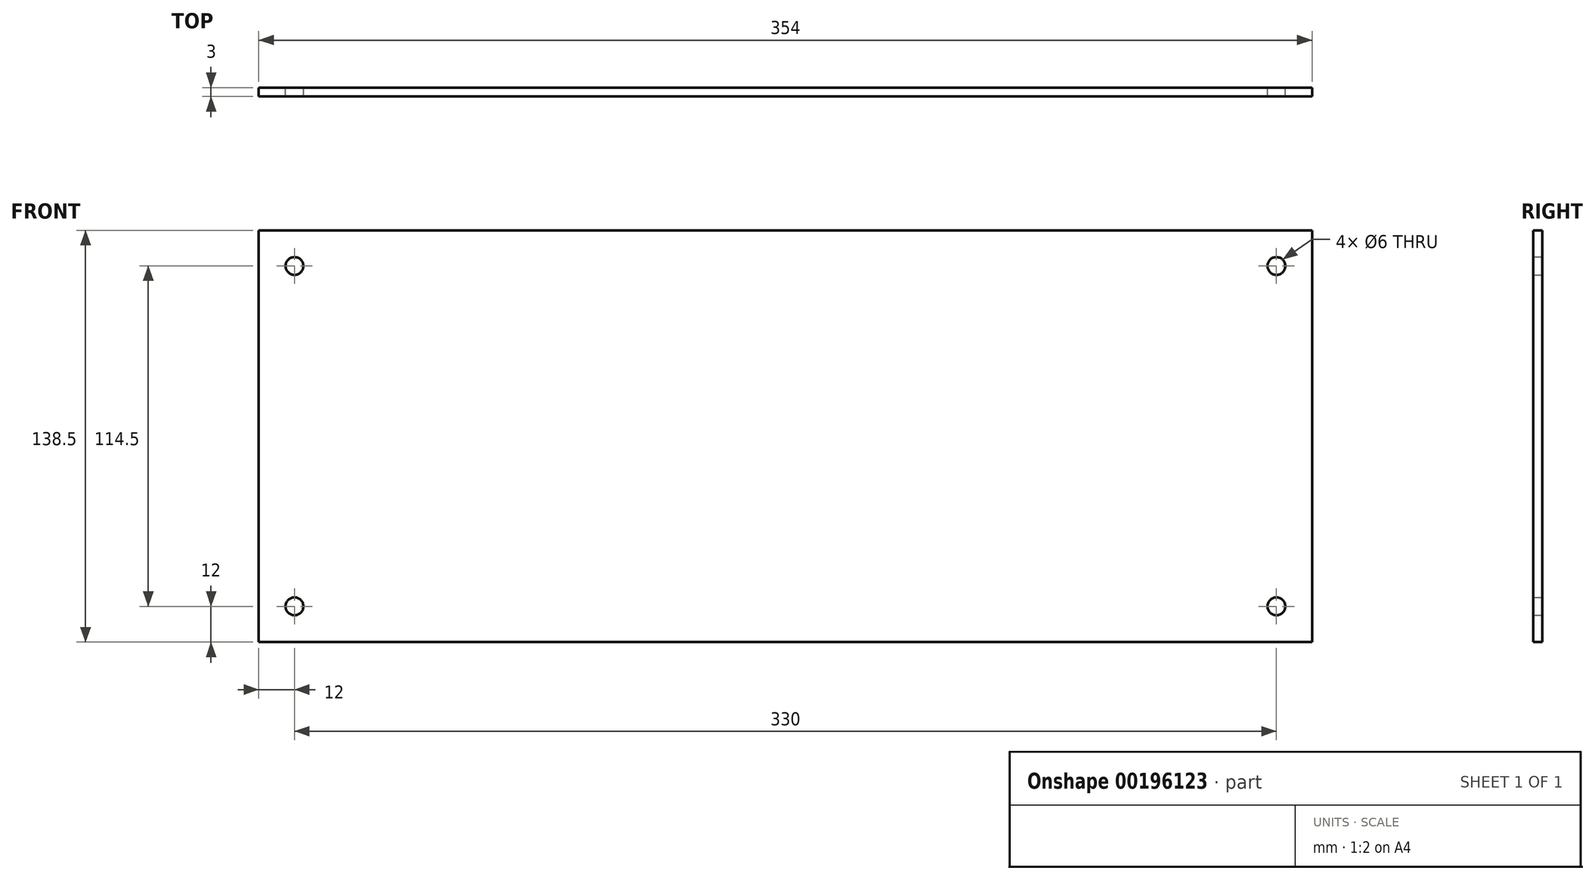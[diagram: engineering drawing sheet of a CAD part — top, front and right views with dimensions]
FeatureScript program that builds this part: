
annotation { "Feature Type Name" : "Feature", "Feature Type Description" : "" }
export const myFeature = defineFeature(function(context is Context, id is Id, definition is map)
    precondition{}
    {
        {
            var Q0;
            Q0=qCreatedBy(makeId("Front.planeOp"),FACE);
            var sketch = newSketch(context, id + "F0", { "sketchPlane" : qUnion([Q0])});
            skLineSegment(sketch, "E0.bottom", {"start": v(177, -69.25) * mm, "end": v(-177, -69.25) * mm});
            skLineSegment(sketch, "E0.top", {"start": v(177, 69.25) * mm, "end": v(-177, 69.25) * mm});
            skLineSegment(sketch, "E0.left", {"start": v(177, -69.25) * mm, "end": v(177, 69.25) * mm});
            skLineSegment(sketch, "E0.right", {"start": v(-177, -69.25) * mm, "end": v(-177, 69.25) * mm});
            skPoint(sketch, "E0.middle", {"position": v(0, 0) * mm});
            skSolve(sketch);
        }
        {
            var Q0;
            Q0 = qSketchRegion(id + "F0", true);
            extrude(context, id + "F1", {"entities" : qUnion([Q0]), "endBound" : BoundingType.SYMMETRIC, "depth" : 3 * mm});
        }
        {
            var Q0;
            Q0=qCreatedBy(makeId("Front.planeOp"),FACE);
            var sketch = newSketch(context, id + "F2", { "sketchPlane" : qUnion([Q0])});
            skLineSegment(sketch, "E1.0", {"start": v(165, 57.25) * mm, "end": v(-165, 57.25) * mm, "construction": true});
            skLineSegment(sketch, "E1.1", {"start": v(165, -57.25) * mm, "end": v(165, 57.25) * mm, "construction": true});
            skLineSegment(sketch, "E1.2", {"start": v(165, -57.25) * mm, "end": v(-165, -57.25) * mm, "construction": true});
            skLineSegment(sketch, "E1.3", {"start": v(-165, -57.25) * mm, "end": v(-165, 57.25) * mm, "construction": true});
            skCircle(sketch, "E2", {"center": v(-165, 57.25) * mm, "radius": 3 * mm});
            skCircle(sketch, "E3", {"center": v(-165, -57.25) * mm, "radius": 3 * mm});
            skCircle(sketch, "E4", {"center": v(165, 57.25) * mm, "radius": 3 * mm});
            skCircle(sketch, "E5", {"center": v(165, -57.25) * mm, "radius": 3 * mm});
            skSolve(sketch);
        }
        {
            var Q0;
            Q0 = qSketchRegion(id + "F2", true);
            extrude(context, id + "F3", {"entities" : qUnion([Q0]), "operationType" : NewBodyOperationType.REMOVE, "endBound" : BoundingType.SYMMETRIC, "depth" : 25 * mm});
        }
    });
